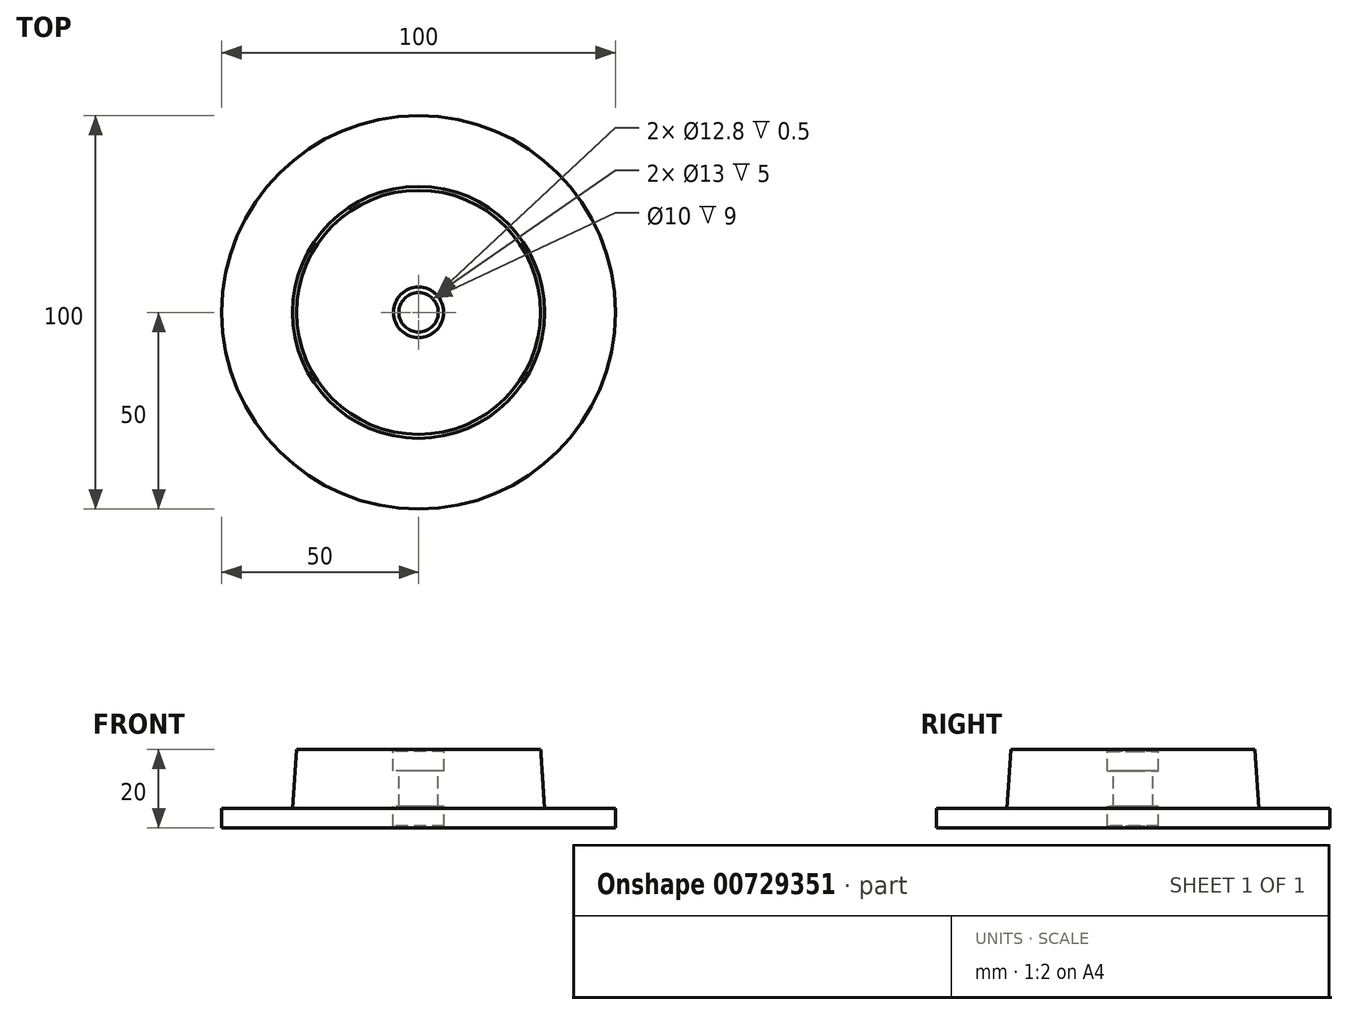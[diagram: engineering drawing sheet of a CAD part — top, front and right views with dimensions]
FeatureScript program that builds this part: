
annotation { "Feature Type Name" : "Feature", "Feature Type Description" : "" }
export const myFeature = defineFeature(function(context is Context, id is Id, definition is map)
    precondition{}
    {
        {
            var Q0;
            Q0=qCreatedBy(makeId("Right.planeOp"),FACE);
            var sketch = newSketch(context, id + "F0", { "sketchPlane" : qUnion([Q0])});
            skLineSegment(sketch, "E0", {"start": v(-6.4, 0) * mm, "end": v(-6.4, 0.5) * mm});
            skLineSegment(sketch, "E1", {"start": v(-6.4, 0.5) * mm, "end": v(-6.5, 0.5) * mm});
            skLineSegment(sketch, "E2", {"start": v(-6.5, 0.5) * mm, "end": v(-6.5, 5.5) * mm});
            skLineSegment(sketch, "E3", {"start": v(-6.5, 5.5) * mm, "end": v(-5, 5.5) * mm});
            skLineSegment(sketch, "E4", {"start": v(-5, 5.5) * mm, "end": v(-5, 14.5) * mm});
            skLineSegment(sketch, "E5", {"start": v(-5, 14.5) * mm, "end": v(-6.5, 14.5) * mm});
            skLineSegment(sketch, "E6", {"start": v(-6.5, 14.5) * mm, "end": v(-6.5, 19.5) * mm});
            skLineSegment(sketch, "E7", {"start": v(-6.5, 19.5) * mm, "end": v(-6.4, 19.5) * mm});
            skLineSegment(sketch, "E8", {"start": v(-6.4, 19.5) * mm, "end": v(-6.4, 20) * mm});
            skLineSegment(sketch, "E9", {"start": v(-6.4, 20) * mm, "end": v(-31, 20) * mm});
            skLineSegment(sketch, "E10", {"start": v(-31, 20) * mm, "end": v(-32, 5) * mm});
            skLineSegment(sketch, "E11", {"start": v(-32, 5) * mm, "end": v(-50, 5) * mm});
            skLineSegment(sketch, "E12", {"start": v(-50, 5) * mm, "end": v(-50, 0) * mm});
            skLineSegment(sketch, "E13", {"start": v(-50, 0) * mm, "end": v(-6.4, 0) * mm});
            skLineSegment(sketch, "E14", {"start": v(-31, 23.45) * mm, "end": v(-31, 12.96) * mm, "construction": true});
            skLineSegment(sketch, "E15", {"start": v(-32, 5.19) * mm, "end": v(-32, -6.44) * mm, "construction": true});
            skLineSegment(sketch, "E16", {"start": v(0, 27.27) * mm, "end": v(0, -9.63) * mm, "construction": true});
            skSolve(sketch);
        }
        {
            var Q0;
            Q0=makeQuery(id+"F0.imprint","IMPRINT",FACE,{"disambiguationData":[TD([[makeQuery(id+"F0.imprint","IMPRINT",EDGE,{"derivedFrom":sQuery(id+"F0.wireOp",EDGE,"E0")}),1.0]])]});
            var Q1;
            Q1=sQuery(id+"F0.wireOp",EDGE,"E16");
            revolve(context, id + "F1", {"surfaceOperationType" : NewSurfaceOperationType.NEW, "entities" : qUnion([Q0]), "axis" : qUnion([Q1]), "revolveType" : RevolveType.FULL});
        }
    });
